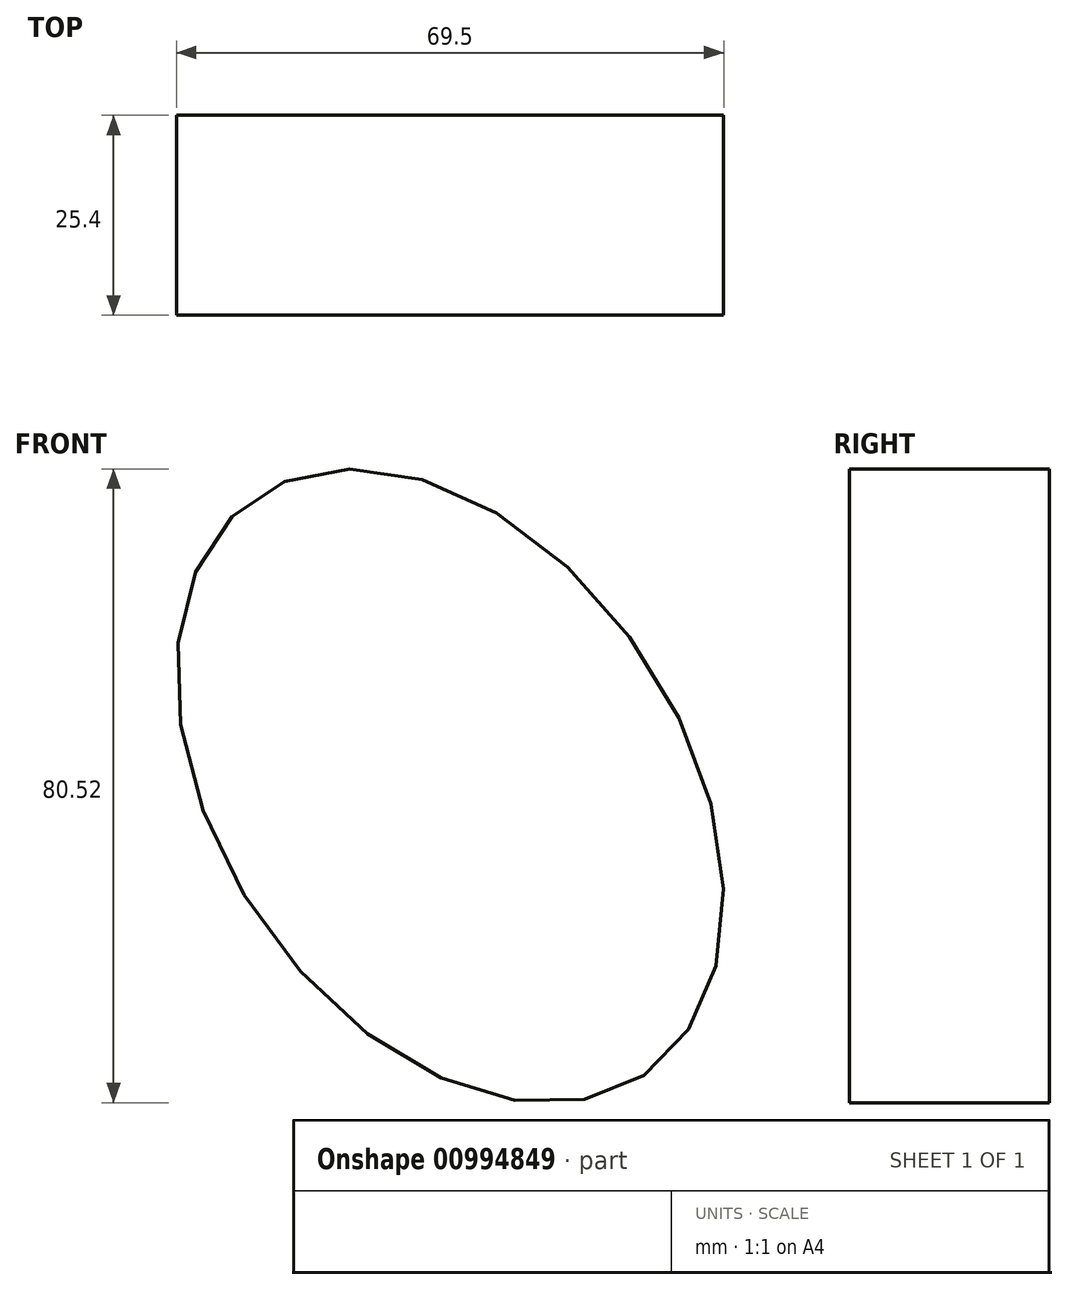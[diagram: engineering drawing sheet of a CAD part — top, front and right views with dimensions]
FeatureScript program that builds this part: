
annotation { "Feature Type Name" : "Feature", "Feature Type Description" : "" }
export const myFeature = defineFeature(function(context is Context, id is Id, definition is map)
    precondition{}
    {
        {
            var Q0;
            Q0=qCreatedBy(makeId("Front.planeOp"),FACE);
            var sketch = newSketch(context, id + "F0", { "sketchPlane" : qUnion([Q0])});
            skEllipse(sketch, "E0", {"center": v(60.43, 0) * mm, "majorRadius": 44.23 * mm, "minorRadius": 29.53 * mm, "majorAxis": v(0.56, -0.83)});
            skSolve(sketch);
        }
        {
            var Q0;
            Q0 = qSketchRegion(id + "F0", true);
            extrude(context, id + "F1", {"entities" : qUnion([Q0]), "depth" : 25.4 * mm, "offsetDistance" : 25.4 * mm});
        }
    });
